# Revit family: Enchufe cerrado 200_250V
name_source: partatom
category: Installations électriques
revit_build: Autodesk Revit 2018 (Build: 20170223_1515(x64)
units: mm (PartAtom-declared; Revit-internal decimal feet)

## family parameters
Conserver l'orientation des annotations = Non
Cote de connecteur circulaire = Utiliser le diamètre
Couper avec des vides une fois chargée = Non
Hôte = Face
Partagée = Non
Point de calcul de pièce = Non
Type d'élément = Normal

## types (2) — shared parameters
Elévation par défaut = 1000 mm  [stored 3.28084 ft]
Estándar CEI o NFC = CEI
Fabricant = Legrand
Familia produce = 0852-P17
Temperatura maxima de uso = +40
Temperatura minima de uso = -25
Tension V = 230 V  50/60 Hz azul
Toma estándar internacional para montaje empotrado o montaje en superficie con accesorio permite la conexión de dispositivos de alimentación = Toma estándar internacional para montaje empotrado o montaje en superficie con accesorio permite la conexión de dispositivos de alimentación
altura mm = 105 mm  [stored 0.344488 ft]
ancho mm = 125 mm  [stored 0.410105 ft]
color característico = azul
distancia de fijación horizontal mm = 91 mm
distancia de fijación vertical mm = 87 mm
intensidad A = 16 A
materia de la caja = plástico
numero de polos = 3
posición de la tierra h = 6
profundidad de empotrar mm = 81 mm  [stored 0.265748 ft]
profundidad mm = 120 mm  [stored 0.393701 ft]
sin halogeno = Oui
tipo de conexión = conexión por tonillo
tipo de enclavamiento = enclavamiento eléctrico y mecánico

## per-type parameters (varying)
| type | Description | Modèle | clase de protección IP | resistencia a los choques IK |
| P17 - IP44 - 200/250V - 16A -2P+T | LG-0357320 Enchufe cerrado P17 - IP55 - 200/250V - 16A -2P+T | LG-057320 | IP55 | 11 |
| P17 - IP55 - 200/250V - 16A -2P+T | LG-0357300 Enchufe cerrado P17 - IP44 - 200/250V - 16A -2P+T | LG-057300 | IP44 | 08 |

note: [stored X ft] marks values corroborated as IEEE doubles in the binary element streams (Revit-internal decimal feet)
